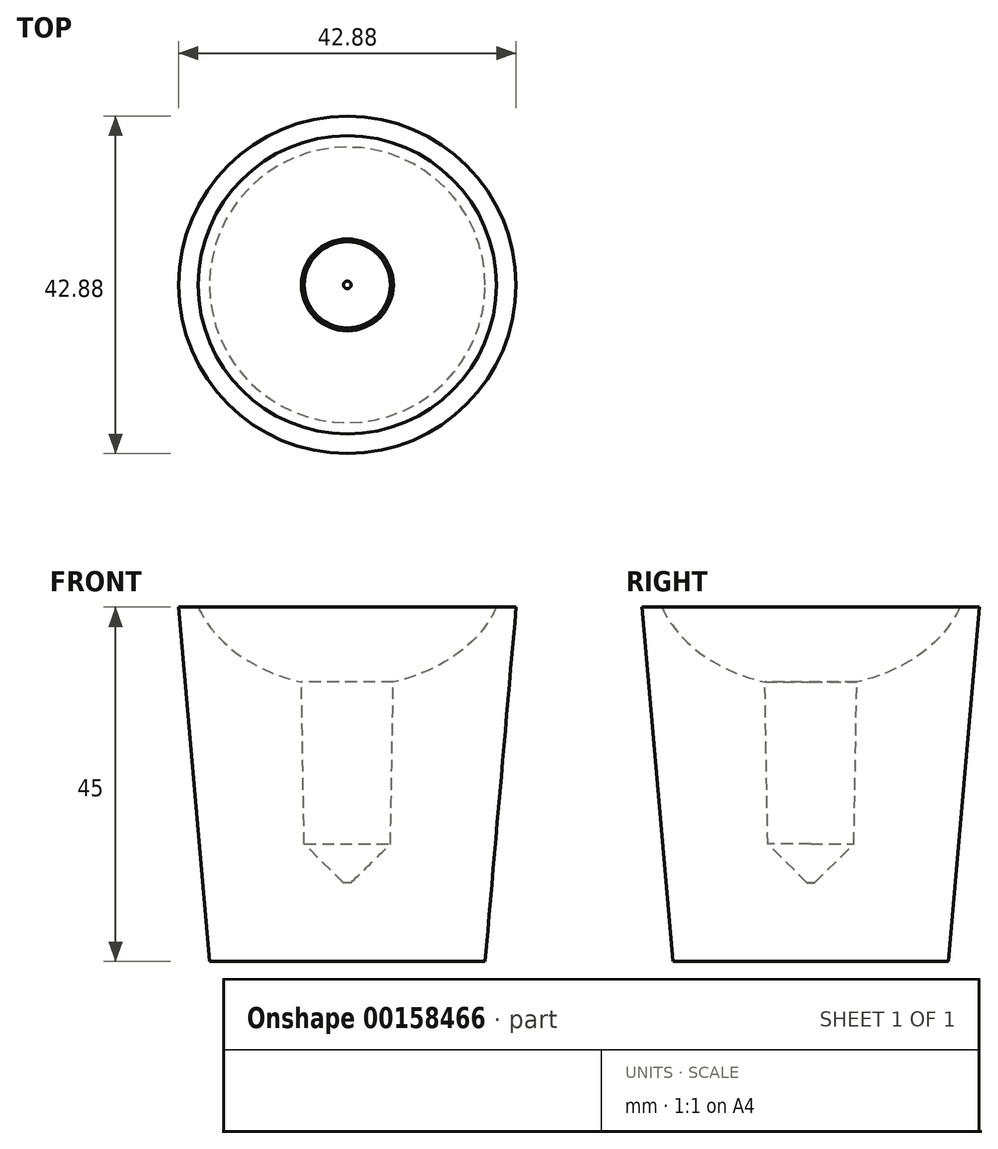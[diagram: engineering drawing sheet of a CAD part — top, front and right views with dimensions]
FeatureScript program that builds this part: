
annotation { "Feature Type Name" : "Feature", "Feature Type Description" : "" }
export const myFeature = defineFeature(function(context is Context, id is Id, definition is map)
    precondition{}
    {
        {
            var Q0;
            Q0=qCreatedBy(makeId("Top.planeOp"),FACE);
            var sketch = newSketch(context, id + "F0", { "sketchPlane" : qUnion([Q0])});
            skCircle(sketch, "E0", {"center": v(0, 0) * mm, "radius": 17.5 * mm});
            skSolve(sketch);
        }
        {
            var Q0;
            Q0=makeQuery(id+"F0.imprint","IMPRINT",FACE,{"disambiguationData":[TD([[makeQuery(id+"F0.imprint","IMPRINT",EDGE,{"derivedFrom":sQuery(id+"F0.wireOp",EDGE,"E0")}),1.0]])]});
            extrude(context, id + "F1", {"entities" : qUnion([Q0]), "depth" : 45 * mm, "hasDraft" : true, "draftAngle" : 5 * degree});
        }
        {
            var Q0;
            Q0=qCreatedBy(makeId("Front.planeOp"),FACE);
            var sketch = newSketch(context, id + "F2", { "sketchPlane" : qUnion([Q0])});
            skLineSegment(sketch, "E1", {"start": v(0, 0) * mm, "end": v(0, 79.1) * mm, "construction": true});
            skEllipticalArc(sketch, "E2", {});
            skLineSegment(sketch, "E3.0", {"start": v(-21.44, 45) * mm, "end": v(21.44, 45) * mm, "construction": true});
            skPoint(sketch, "E4", {"position": v(-18.94, 45) * mm});
            skLineSegment(sketch, "E5", {"start": v(0, 34.83) * mm, "end": v(0, 64.83) * mm});
            const initialGuessF2  = {"E2": [0, 0.04982515372705129, 0, -1, 0.015, 0.02, 3.141592653589793, 6.283185307179586]};
            skSetInitialGuess(sketch, initialGuessF2);
            skSolve(sketch);
        }
        {
            var Q0;
            Q0=makeQuery(id+"F1.opExtrude","CAP_FACE",FACE,{"disambiguationData":[OSD([sQuery(id+"F0.wireOp",EDGE,"E0")])],"isStart":false});
            var sketch = newSketch(context, id + "F3", { "sketchPlane" : qUnion([Q0])});
            skCircle(sketch, "E6", {"center": v(0, 0) * mm, "radius": 6 * mm});
            skSolve(sketch);
        }
        {
            var Q0;
            Q0=makeQuery(id+"F3.imprint","IMPRINT",FACE,{"disambiguationData":[TD([[makeQuery(id+"F3.imprint","IMPRINT",EDGE,{"derivedFrom":sQuery(id+"F3.wireOp",EDGE,"E6")}),1.0]])]});
            extrude(context, id + "F4", {"entities" : qUnion([Q0]), "operationType" : NewBodyOperationType.REMOVE, "oppositeDirection" : true, "depth" : 35 * mm, "hasDraft" : true, "draftAngle" : 1 * degree, "draftPullDirection" : true});
        }
        {
            var Q0;
            Q0=makeQuery(id+"F4.boolean.opBoolean","COPY",EDGE,{"derivedFrom":makeQuery(id+"F4.opExtrude","CAP_EDGE",EDGE,{"disambiguationData":[OSD([sQuery(id+"F3.wireOp",EDGE,"E6")])],"isStart":false})});
            chamfer(context, id + "F5", {"entities" : qUnion([Q0]), "width" : 5 * mm, "tangentPropagation" : true});
        }
        {
            var Q0;
            Q0=makeQuery(id+"F2.imprint","IMPRINT",FACE,{"disambiguationData":[TD([[makeQuery(id+"F2.imprint","IMPRINT",EDGE,{"derivedFrom":sQuery(id+"F2.wireOp",EDGE,"E2")}),1.0]])]});
            var Q1;
            Q1=sQuery(id+"F2.wireOp",EDGE,"E1");
            revolve(context, id + "F6", {"operationType" : NewBodyOperationType.REMOVE, "entities" : qUnion([Q0]), "axis" : qUnion([Q1]), "revolveType" : RevolveType.FULL, "oppositeDirection" : true});
        }
    });
